# Revit family: LAMP_MICROSHOT G2
name_source: partatom
category: Modelos genéricos
revit_build: Autodesk Revit 2015 (Build: 20140606_1530(x64)
units: mm (PartAtom-declared; Revit-internal decimal feet)

## types (8) — shared parameters
CRI = 80
Comentarios de tipo = Availability of tilting between -30º and 90º when placed in a project.
Diameter = 80 mm  [stored 0.262467 ft]
Elevación por defecto = 1219 mm
Fabricante = LAMP
Gear = Electronic
Height = 161 mm  [stored 0.528215 ft]
IEE = A+
Installation instructions = http://www.lamp.es
Insulation class = III
LED Lifetime = 60.000 L90 B10
Lamp = HIGH POWER LED
Last update = 11/04/2019
Luminaire type = Outdoor - Spotlight
MacAdam = 3
Manufacturer URL = http://www.lamp.es
Manufacturer country = Spain
Manufacturer name = LAMP
Model explanation = Availability of tilting between -30º and 90º when placed in a project.
Power = 6 W
Power Supply = 700mA DC
Product URL = http://www.lamp.es
Product datasheet = http://www.lamp.es
Protection rating = IP65 / IK06
Type = HI POWER NICHIA
Weight = 0.71 kg

## per-type parameters (varying)
| type | Descripción | Finish | Initial color | Initial intensity | Material cabeza | Material cuerpo | Modelo | Photometric web file | Product code |
| 609LM 3000 MEDIUM FLOOD ANT | MICRO SHOT G2 900 WW MFL NO GEAR ANT. | Textured anthracite grey | 3000 K | 609 lm | LAMP_Aluminio Shot Antracita | LAMP_Aluminio Shot Antracita | MC209MF8300A | Cabeza Microshot : 609LM 3000 MEDIUM FLOOD | MC209MF8300A |
| 609LM 3000 MEDIUM FLOOD GR | MICRO SHOT G2 900 WW MFL NO GEAR GR. | Texturised grey | 3000 K | 609 lm | LAMP_Aluminio Shot | LAMP_Aluminio Shot | MC209MF8300G | Cabeza Microshot : 609LM 3000 MEDIUM FLOOD | MC209MF8300G |
| 609LM 4000 MEDIUM FLOOD ANT | MICRO SHOT G2 900 NW MFL NO GEAR ANT. | Textured anthracite grey | 4000 K | 609 lm | LAMP_Aluminio Shot Antracita | LAMP_Aluminio Shot Antracita | MC209MF8400A | Cabeza Microshot : 609LM 4000 MEDIUM FLOOD | MC209MF8400A |
| 609LM 4000 MEDIUM FLOOD GR | MICRO SHOT G2 900 NW MFL NO GEAR GR. | Texturised grey | 4000 K | 609 lm | LAMP_Aluminio Shot | LAMP_Aluminio Shot | MC209MF8400G | Cabeza Microshot : 609LM 4000 MEDIUM FLOOD | MC209MF8400G |
| 720LM 3000 SPOT ANT | MICRO SHOT G2 900 WW SP NO GEAR ANT. | Textured anthracite grey | 3000 K | 720 lm | LAMP_Aluminio Shot Antracita | LAMP_Aluminio Shot Antracita | MC209SP8300A | Cabeza Microshot : 720LM 3000 SPOT | MC209SP8300A |
| 720LM 3000 SPOT GR | MICRO SHOT G2 900 WW SP NO GEAR GR. | Texturised grey | 3000 K | 720 lm | LAMP_Aluminio Shot | LAMP_Aluminio Shot | MC209SP8300G | Cabeza Microshot : 720LM 3000 SPOT | MC209SP8300G |
| 720LM 4000 SPOT ANT | MICRO SHOT G2 900 NW SP NO GEAR ANT. | Textured anthracite grey | 4000 K | 720 lm | LAMP_Aluminio Shot Antracita | LAMP_Aluminio Shot Antracita | MC209SP8400A | Cabeza Microshot : 720LM 4000 SPOT | MC209SP8400A |
| 720LM 4000 SPOT GR | MICRO SHOT G2 900 NW SP NO GEAR GR. | Texturised grey | 4000 K | 720 lm | LAMP_Aluminio Shot | LAMP_Aluminio Shot | MC209SP8400G | Cabeza Microshot : 720LM 4000 SPOT | MC209SP8400G |

note: [stored X ft] marks values corroborated as IEEE doubles in the binary element streams (Revit-internal decimal feet)
